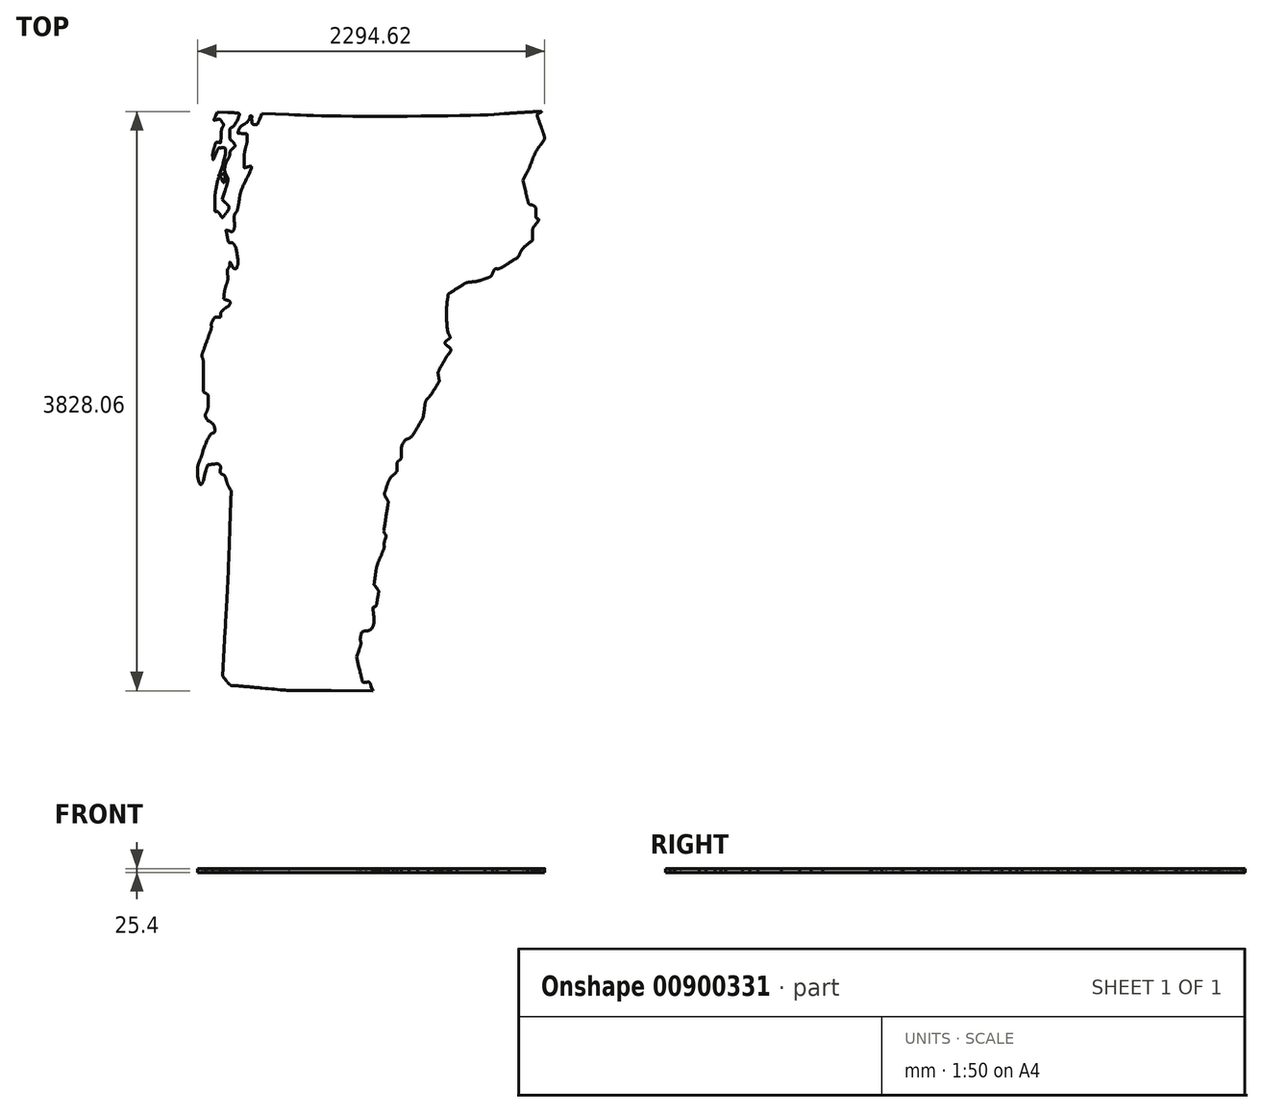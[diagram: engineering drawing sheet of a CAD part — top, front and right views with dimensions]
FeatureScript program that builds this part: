
annotation { "Feature Type Name" : "Feature", "Feature Type Description" : "" }
export const myFeature = defineFeature(function(context is Context, id is Id, definition is map)
    precondition{}
    {
        {
            var Q0;
            Q0=qCreatedBy(makeId("Top.planeOp"),FACE);
            var sketch = newSketch(context, id + "F0", { "sketchPlane" : qUnion([Q0])});
            skLineSegment(sketch, "E0", {"start": v(-2148.42, -1753.94) * mm, "end": v(-2163.83, -1690.8) * mm});
            skLineSegment(sketch, "E1", {"start": v(-2163.83, -1690.8) * mm, "end": v(-2148.01, -1646.42) * mm});
            skLineSegment(sketch, "E2", {"start": v(-1045.74, 1382.66) * mm, "end": v(-1065.36, 1461.75) * mm});
            skLineSegment(sketch, "E3", {"start": v(-1065.36, 1461.75) * mm, "end": v(-1044.06, 1499.75) * mm});
            skLineSegment(sketch, "E4", {"start": v(-2608.76, 1895.1) * mm, "end": v(-2788.04, 1901.18) * mm});
            skLineSegment(sketch, "E5", {"start": v(-2788.04, 1901.18) * mm, "end": v(-2803.72, 1864.08) * mm});
            skLineSegment(sketch, "E6", {"start": v(-3031.83, -1515.3) * mm, "end": v(-3049.52, -1815.66) * mm});
            skLineSegment(sketch, "E7", {"start": v(-3049.52, -1815.66) * mm, "end": v(-3023.97, -1846.84) * mm});
            skLineSegment(sketch, "E8", {"start": v(-2331.5, -1913) * mm, "end": v(-2054.3, -1913.86) * mm});
            skLineSegment(sketch, "E9", {"start": v(-2054.3, -1913.86) * mm, "end": v(-2065.56, -1885.2) * mm});
            skLineSegment(sketch, "E10", {"start": v(-2065.56, -1885.2) * mm, "end": v(-2065.56, -1885.2) * mm});
            skLineSegment(sketch, "E11", {"start": v(-3014.34, 1908.53) * mm, "end": v(-3083.06, 1911.96) * mm});
            skLineSegment(sketch, "E12", {"start": v(-3083.06, 1911.96) * mm, "end": v(-3092.64, 1889.73) * mm});
            skLineSegment(sketch, "E13", {"start": v(-3034.55, 1231.3) * mm, "end": v(-3034.54, 1231.3) * mm});
            skLineSegment(sketch, "E14", {"start": v(-3034.54, 1231.3) * mm, "end": v(-3034.55, 1231.3) * mm});
            skLineSegment(sketch, "E15", {"start": v(-3028.42, 1311.2) * mm, "end": v(-3050.3, 1333.08) * mm});
            skLineSegment(sketch, "E16", {"start": v(-3050.3, 1333.08) * mm, "end": v(-3032, 1390.98) * mm});
            skLineSegment(sketch, "E17", {"start": v(-3014.1, 1468.22) * mm, "end": v(-3030.96, 1512.32) * mm});
            skLineSegment(sketch, "E18", {"start": v(-3030.96, 1512.32) * mm, "end": v(-3014.1, 1468.22) * mm});
            skLineSegment(sketch, "E19", {"start": v(-3017.3, 1591.5) * mm, "end": v(-3017.3, 1591.5) * mm});
            skFitSpline(sketch, "E20", {"points": [v(-2065.56, -1885.2) * mm, v(-2075.06, -1861) * mm, v(-2080.05, -1856.52) * mm, v(-2097.42, -1856.52) * mm]});
            skFitSpline(sketch, "E21", {"points": [v(-2097.42, -1856.52) * mm, v(-2121.49, -1856.52) * mm, v(-2125.24, -1848.98) * mm, v(-2148.42, -1753.94) * mm]});
            skFitSpline(sketch, "E22", {"points": [v(-2148.01, -1646.42) * mm, v(-2139.32, -1622) * mm, v(-2134, -1595.32) * mm, v(-2136.2, -1587.12) * mm]});
            skFitSpline(sketch, "E23", {"points": [v(-2136.2, -1587.12) * mm, v(-2138.4, -1578.92) * mm, v(-2137.39, -1561.34) * mm, v(-2133.95, -1548.06) * mm]});
            skFitSpline(sketch, "E24", {"points": [v(-2133.95, -1548.06) * mm, v(-2129.08, -1529.28) * mm, v(-2122.72, -1522.62) * mm, v(-2105.34, -1518.12) * mm]});
            skFitSpline(sketch, "E25", {"points": [v(-2105.34, -1518.12) * mm, v(-2069.8, -1508.9) * mm, v(-2047.58, -1462.63) * mm, v(-2051.65, -1406.32) * mm]});
            skFitSpline(sketch, "E26", {"points": [v(-2051.65, -1406.32) * mm, v(-2054.2, -1371.05) * mm, v(-2052.62, -1361.24) * mm, v(-2043.8, -1357.86) * mm]});
            skFitSpline(sketch, "E27", {"points": [v(-2043.8, -1357.86) * mm, v(-2036.62, -1355.1) * mm, v(-2029.83, -1336.31) * mm, v(-2024.4, -1304.17) * mm]});
            skFitSpline(sketch, "E28", {"points": [v(-2024.4, -1304.17) * mm, v(-2016.57, -1257.68) * mm, v(-2017, -1253.42) * mm, v(-2031.72, -1232.75) * mm]});
            skFitSpline(sketch, "E29", {"points": [v(-2031.72, -1232.75) * mm, v(-2046.73, -1211.67) * mm, v(-2047.02, -1208.2) * mm, v(-2038.74, -1148.34) * mm]});
            skFitSpline(sketch, "E30", {"points": [v(-2038.74, -1148.34) * mm, v(-2033.05, -1107.24) * mm, v(-2021.43, -1066.31) * mm, v(-2004.72, -1028.56) * mm]});
            skFitSpline(sketch, "E31", {"points": [v(-2004.72, -1028.56) * mm, v(-1990.76, -997.02) * mm, v(-1979.84, -963.26) * mm, v(-1980.45, -953.54) * mm]});
            skFitSpline(sketch, "E32", {"points": [v(-1980.45, -953.54) * mm, v(-1981.06, -943.82) * mm, v(-1978.14, -925.5) * mm, v(-1973.95, -912.84) * mm]});
            skFitSpline(sketch, "E33", {"points": [v(-1973.95, -912.84) * mm, v(-1968.31, -895.74) * mm, v(-1968.62, -886.18) * mm, v(-1975.17, -875.7) * mm]});
            skFitSpline(sketch, "E34", {"points": [v(-1975.17, -875.7) * mm, v(-1982.3, -864.27) * mm, v(-1981.02, -842.87) * mm, v(-1968.46, -763.57) * mm]});
            skFitSpline(sketch, "E35", {"points": [v(-1968.46, -763.57) * mm, v(-1954.46, -675.2) * mm, v(-1953.98, -663.53) * mm, v(-1963.61, -644.9) * mm]});
            skFitSpline(sketch, "E36", {"points": [v(-1963.61, -644.9) * mm, v(-1977.63, -617.8) * mm, v(-1977.12, -606.03) * mm, v(-1959.68, -554.4) * mm]});
            skFitSpline(sketch, "E37", {"points": [v(-1959.68, -554.4) * mm, v(-1950.52, -527.27) * mm, v(-1935.82, -502.16) * mm, v(-1920.26, -487.08) * mm]});
            skFitSpline(sketch, "E38", {"points": [v(-1920.26, -487.08) * mm, v(-1899.8, -467.25) * mm, v(-1895.44, -457.8) * mm, v(-1895.44, -433.29) * mm]});
            skFitSpline(sketch, "E39", {"points": [v(-1895.44, -433.29) * mm, v(-1895.44, -412.65) * mm, v(-1891.05, -399.57) * mm, v(-1881.1, -390.57) * mm]});
            skFitSpline(sketch, "E40", {"points": [v(-1881.1, -390.57) * mm, v(-1870.92, -381.35) * mm, v(-1866.77, -368.5) * mm, v(-1866.77, -346.16) * mm]});
            skFitSpline(sketch, "E41", {"points": [v(-1866.77, -346.16) * mm, v(-1866.77, -307) * mm, v(-1843.82, -260.57) * mm, v(-1816.8, -245.06) * mm]});
            skFitSpline(sketch, "E42", {"points": [v(-1816.8, -245.06) * mm, v(-1804.9, -238.24) * mm, v(-1781.25, -207.78) * mm, v(-1760.1, -172.05) * mm]});
            skFitSpline(sketch, "E43", {"points": [v(-1760.1, -172.05) * mm, v(-1730.1, -121.38) * mm, v(-1722.35, -100.98) * mm, v(-1715.43, -54.43) * mm]});
            skFitSpline(sketch, "E44", {"points": [v(-1715.43, -54.43) * mm, v(-1709.02, -11.34) * mm, v(-1702.54, 7.17) * mm, v(-1687.85, 24.3) * mm]});
            skFitSpline(sketch, "E45", {"points": [v(-1687.85, 24.3) * mm, v(-1677.3, 36.62) * mm, v(-1656.9, 65.75) * mm, v(-1642.55, 89.03) * mm]});
            skFitSpline(sketch, "E46", {"points": [v(-1642.55, 89.03) * mm, v(-1619.85, 125.83) * mm, v(-1617, 135.35) * mm, v(-1620.65, 162) * mm]});
            skFitSpline(sketch, "E47", {"points": [v(-1620.65, 162) * mm, v(-1624.26, 188.36) * mm, v(-1621.07, 199.45) * mm, v(-1597.76, 241.53) * mm]});
            skFitSpline(sketch, "E48", {"points": [v(-1597.76, 241.53) * mm, v(-1582.87, 268.43) * mm, v(-1564.72, 299) * mm, v(-1557.43, 309.46) * mm]});
            skFitSpline(sketch, "E49", {"points": [v(-1557.43, 309.46) * mm, v(-1540.47, 333.83) * mm, v(-1540.72, 346) * mm, v(-1558.52, 362.12) * mm]});
            skFitSpline(sketch, "E50", {"points": [v(-1558.52, 362.12) * mm, v(-1576.84, 378.69) * mm, v(-1576.7, 392.56) * mm, v(-1558.05, 407.65) * mm]});
            skFitSpline(sketch, "E51", {"points": [v(-1558.05, 407.65) * mm, v(-1545, 418.22) * mm, v(-1544.26, 422.18) * mm, v(-1551.79, 441.06) * mm]});
            skFitSpline(sketch, "E52", {"points": [v(-1551.79, 441.06) * mm, v(-1560.89, 463.86) * mm, v(-1567.15, 628.71) * mm, v(-1560.83, 678.8) * mm]});
            skFitSpline(sketch, "E53", {"points": [v(-1560.83, 678.8) * mm, v(-1557.24, 707.23) * mm, v(-1554.07, 710.66) * mm, v(-1498.64, 746) * mm]});
            skFitSpline(sketch, "E54", {"points": [v(-1498.64, 746) * mm, v(-1452.27, 775.56) * mm, v(-1431.38, 784.36) * mm, v(-1397.23, 788.76) * mm]});
            skFitSpline(sketch, "E55", {"points": [v(-1397.23, 788.76) * mm, v(-1373.57, 791.8) * mm, v(-1336.26, 801.1) * mm, v(-1314.32, 809.41) * mm]});
            skFitSpline(sketch, "E56", {"points": [v(-1314.32, 809.41) * mm, v(-1282.53, 821.45) * mm, v(-1271.99, 829.62) * mm, v(-1262.46, 849.6) * mm]});
            skFitSpline(sketch, "E57", {"points": [v(-1262.46, 849.6) * mm, v(-1254.04, 867.25) * mm, v(-1245.7, 874.7) * mm, v(-1234.26, 874.78) * mm]});
            skFitSpline(sketch, "E58", {"points": [v(-1234.26, 874.78) * mm, v(-1225.33, 874.85) * mm, v(-1190.6, 892.04) * mm, v(-1157.09, 913) * mm]});
            skFitSpline(sketch, "E59", {"points": [v(-1157.09, 913) * mm, v(-1109.24, 942.9) * mm, v(-1093.08, 957.4) * mm, v(-1081.82, 980.47) * mm]});
            skFitSpline(sketch, "E60", {"points": [v(-1081.82, 980.47) * mm, v(-1073.93, 996.64) * mm, v(-1052.17, 1022.18) * mm, v(-1033.46, 1037.24) * mm]});
            skFitSpline(sketch, "E61", {"points": [v(-1033.46, 1037.24) * mm, v(-1000.4, 1063.85) * mm, v(-999.43, 1065.74) * mm, v(-999.2, 1104.05) * mm]});
            skFitSpline(sketch, "E62", {"points": [v(-999.2, 1104.05) * mm, v(-999.02, 1136.53) * mm, v(-995.2, 1148.47) * mm, v(-977.56, 1171.8) * mm]});
            skFitSpline(sketch, "E63", {"points": [v(-977.56, 1171.8) * mm, v(-959.49, 1195.68) * mm, v(-957.83, 1201.07) * mm, v(-967, 1206.2) * mm]});
            skFitSpline(sketch, "E64", {"points": [v(-967, 1206.2) * mm, v(-974.09, 1210.17) * mm, v(-977.88, 1223.01) * mm, v(-977.88, 1243.08) * mm]});
            skFitSpline(sketch, "E65", {"points": [v(-977.88, 1243.08) * mm, v(-977.88, 1273.86) * mm, v(-988.6, 1290.36) * mm, v(-1014.54, 1299.5) * mm]});
            skFitSpline(sketch, "E66", {"points": [v(-1014.54, 1299.5) * mm, v(-1022.4, 1302.27) * mm, v(-1032.41, 1328.94) * mm, v(-1045.74, 1382.66) * mm]});
            skFitSpline(sketch, "E67", {"points": [v(-1044.06, 1499.75) * mm, v(-1032.34, 1520.64) * mm, v(-1013.81, 1561.94) * mm, v(-1002.88, 1591.5) * mm]});
            skFitSpline(sketch, "E68", {"points": [v(-1002.88, 1591.5) * mm, v(-991.95, 1621.07) * mm, v(-968.95, 1664.42) * mm, v(-951.77, 1687.83) * mm]});
            skFitSpline(sketch, "E69", {"points": [v(-951.77, 1687.83) * mm, v(-934.58, 1711.24) * mm, v(-920.53, 1734.37) * mm, v(-920.53, 1739.23) * mm]});
            skFitSpline(sketch, "E70", {"points": [v(-920.53, 1739.23) * mm, v(-920.53, 1744.1) * mm, v(-930.2, 1775.49) * mm, v(-942.03, 1809) * mm]});
            skFitSpline(sketch, "E71", {"points": [v(-942.03, 1809) * mm, v(-966.83, 1879.25) * mm, v(-968.4, 1896.2) * mm, v(-951, 1906.34) * mm]});
            skFitSpline(sketch, "E72", {"points": [v(-951, 1906.34) * mm, v(-940.05, 1912.71) * mm, v(-940.74, 1913.68) * mm, v(-956.37, 1913.86) * mm]});
            skFitSpline(sketch, "E73", {"points": [v(-956.37, 1913.86) * mm, v(-966.23, 1913.99) * mm, v(-1056.4, 1909.13) * mm, v(-1156.75, 1903.07) * mm]});
            skFitSpline(sketch, "E74", {"points": [v(-1156.75, 1903.07) * mm, v(-1368.69, 1890.3) * mm, v(-2314.58, 1885.09) * mm, v(-2608.76, 1895.1) * mm]});
            skFitSpline(sketch, "E75", {"points": [v(-2803.72, 1864.08) * mm, v(-2816.9, 1832.88) * mm, v(-2822.03, 1827.34) * mm, v(-2835.91, 1829.3) * mm]});
            skFitSpline(sketch, "E76", {"points": [v(-2835.91, 1829.3) * mm, v(-2849.08, 1831.17) * mm, v(-2853.15, 1837.2) * mm, v(-2856, 1859.1) * mm]});
            skFitSpline(sketch, "E77", {"points": [v(-2872.23, 1865) * mm, v(-2879.18, 1853.15) * mm, v(-2895.83, 1836.68) * mm, v(-2909.23, 1828.4) * mm]});
            skFitSpline(sketch, "E78", {"points": [v(-2909.23, 1828.4) * mm, v(-2922.63, 1820.12) * mm, v(-2936.88, 1803.92) * mm, v(-2940.89, 1792.42) * mm]});
            skFitSpline(sketch, "E79", {"points": [v(-2940.89, 1792.42) * mm, v(-2948.13, 1771.64) * mm, v(-2947.97, 1771.48) * mm, v(-2918.22, 1769.31) * mm]});
            skFitSpline(sketch, "E80", {"points": [v(-2918.22, 1769.31) * mm, v(-2890.43, 1767.29) * mm, v(-2888.1, 1765.5) * mm, v(-2886.08, 1744.6) * mm]});
            skFitSpline(sketch, "E81", {"points": [v(-2886.08, 1744.6) * mm, v(-2884.87, 1732.22) * mm, v(-2888.9, 1702.72) * mm, v(-2895.04, 1679.06) * mm]});
            skFitSpline(sketch, "E82", {"points": [v(-2895.04, 1679.06) * mm, v(-2901.17, 1655.4) * mm, v(-2906.19, 1615.17) * mm, v(-2906.19, 1589.67) * mm]});
            skFitSpline(sketch, "E83", {"points": [v(-2906.19, 1589.67) * mm, v(-2906.19, 1544.15) * mm, v(-2905.86, 1543.38) * mm, v(-2888.36, 1546.72) * mm]});
            skFitSpline(sketch, "E84", {"points": [v(-2888.36, 1546.72) * mm, v(-2858.93, 1552.35) * mm, v(-2860.45, 1533.85) * mm, v(-2895.66, 1458.28) * mm]});
            skFitSpline(sketch, "E85", {"points": [v(-2895.66, 1458.28) * mm, v(-2919.3, 1407.5) * mm, v(-2931.76, 1368.85) * mm, v(-2939.26, 1322.95) * mm]});
            skFitSpline(sketch, "E86", {"points": [v(-2939.26, 1322.95) * mm, v(-2945.03, 1287.6) * mm, v(-2954.47, 1253.48) * mm, v(-2960.23, 1247.11) * mm]});
            skFitSpline(sketch, "E87", {"points": [v(-2960.23, 1247.11) * mm, v(-2966.86, 1239.78) * mm, v(-2970.79, 1219.98) * mm, v(-2970.93, 1193.1) * mm]});
            skFitSpline(sketch, "E88", {"points": [v(-2970.93, 1193.1) * mm, v(-2971.2, 1143.34) * mm, v(-2983.25, 1122.17) * mm, v(-3008.54, 1127) * mm]});
            skFitSpline(sketch, "E89", {"points": [v(-3008.54, 1127) * mm, v(-3025.55, 1130.26) * mm, v(-3025.56, 1130.23) * mm, v(-3017.58, 1090.27) * mm]});
            skFitSpline(sketch, "E90", {"points": [v(-3017.58, 1090.27) * mm, v(-3011.03, 1057.45) * mm, v(-3006.75, 1049.88) * mm, v(-2993.72, 1048) * mm]});
            skFitSpline(sketch, "E91", {"points": [v(-2993.72, 1048) * mm, v(-2984.99, 1046.73) * mm, v(-2974.9, 1040.2) * mm, v(-2971.3, 1033.5) * mm]});
            skFitSpline(sketch, "E92", {"points": [v(-2971.3, 1033.5) * mm, v(-2961.65, 1015.46) * mm, v(-2946.27, 906.96) * mm, v(-2951.45, 893.46) * mm]});
            skFitSpline(sketch, "E93", {"points": [v(-2951.45, 893.46) * mm, v(-2958.29, 875.65) * mm, v(-2976.2, 879.6) * mm, v(-2988.1, 901.54) * mm]});
            skFitSpline(sketch, "E94", {"points": [v(-2988.1, 901.54) * mm, v(-2997.18, 918.27) * mm, v(-2998.88, 919.08) * mm, v(-2999.32, 906.92) * mm]});
            skFitSpline(sketch, "E95", {"points": [v(-2999.32, 906.92) * mm, v(-2999.6, 899.03) * mm, v(-3004.17, 886.87) * mm, v(-3009.46, 879.9) * mm]});
            skFitSpline(sketch, "E96", {"points": [v(-3009.46, 879.9) * mm, v(-3015.64, 871.75) * mm, v(-3017.83, 856) * mm, v(-3015.56, 835.9) * mm]});
            skFitSpline(sketch, "E97", {"points": [v(-3015.56, 835.9) * mm, v(-3013.43, 817.02) * mm, v(-3016.63, 790.73) * mm, v(-3023.6, 769.73) * mm]});
            skFitSpline(sketch, "E98", {"points": [v(-3023.6, 769.73) * mm, v(-3029.96, 750.56) * mm, v(-3036.43, 721.77) * mm, v(-3037.97, 705.76) * mm]});
            skFitSpline(sketch, "E99", {"points": [v(-3037.97, 705.76) * mm, v(-3040.3, 681.44) * mm, v(-3038.25, 675.54) * mm, v(-3025.49, 669.92) * mm]});
            skFitSpline(sketch, "E100", {"points": [v(-3025.49, 669.92) * mm, v(-2999.78, 658.6) * mm, v(-3002.3, 638.08) * mm, v(-3032.5, 612.72) * mm]});
            skFitSpline(sketch, "E101", {"points": [v(-3032.5, 612.72) * mm, v(-3049.94, 598.09) * mm, v(-3060.03, 583.45) * mm, v(-3060.14, 572.66) * mm]});
            skFitSpline(sketch, "E102", {"points": [v(-3060.14, 572.66) * mm, v(-3060.28, 558.85) * mm, v(-3064.15, 555.61) * mm, v(-3080.83, 555.37) * mm]});
            skFitSpline(sketch, "E103", {"points": [v(-3080.83, 555.37) * mm, v(-3096.07, 555.16) * mm, v(-3104.27, 549.62) * mm, v(-3112.7, 533.87) * mm]});
            skFitSpline(sketch, "E104", {"points": [v(-3112.7, 533.87) * mm, v(-3118.95, 522.2) * mm, v(-3123.31, 506.2) * mm, v(-3122.4, 498.32) * mm]});
            skFitSpline(sketch, "E105", {"points": [v(-3122.4, 498.32) * mm, v(-3121.5, 490.43) * mm, v(-3135.56, 443.78) * mm, v(-3153.65, 394.64) * mm]});
            skFitSpline(sketch, "E106", {"points": [v(-3153.65, 394.64) * mm, v(-3178.45, 327.3) * mm, v(-3185.13, 300.82) * mm, v(-3180.8, 287.11) * mm]});
            skFitSpline(sketch, "E107", {"points": [v(-3180.8, 287.11) * mm, v(-3177.65, 277.11) * mm, v(-3175.06, 222.57) * mm, v(-3175.04, 165.91) * mm]});
            skFitSpline(sketch, "E108", {"points": [v(-3175.04, 165.91) * mm, v(-3174.97, 67.07) * mm, v(-3174.35, 62.46) * mm, v(-3158.88, 52.13) * mm]});
            skFitSpline(sketch, "E109", {"points": [v(-3158.88, 52.13) * mm, v(-3145.18, 43) * mm, v(-3142.75, 34.97) * mm, v(-3142.75, -1) * mm]});
            skFitSpline(sketch, "E110", {"points": [v(-3142.75, -1) * mm, v(-3142.75, -24.3) * mm, v(-3147.47, -54.66) * mm, v(-3153.23, -68.46) * mm]});
            skFitSpline(sketch, "E111", {"points": [v(-3153.23, -68.46) * mm, v(-3161.37, -87.94) * mm, v(-3161.92, -97.53) * mm, v(-3155.67, -111.24) * mm]});
            skFitSpline(sketch, "E112", {"points": [v(-3155.67, -111.24) * mm, v(-3151.24, -120.97) * mm, v(-3144.9, -128.92) * mm, v(-3141.6, -128.92) * mm]});
            skFitSpline(sketch, "E113", {"points": [v(-3141.6, -128.92) * mm, v(-3138.29, -128.92) * mm, v(-3129.13, -135.37) * mm, v(-3121.24, -143.26) * mm]});
            skFitSpline(sketch, "E114", {"points": [v(-3121.24, -143.26) * mm, v(-3106.41, -158.09) * mm, v(-3101.18, -203.4) * mm, v(-3113.43, -210.96) * mm]});
            skFitSpline(sketch, "E115", {"points": [v(-3113.43, -210.96) * mm, v(-3128.05, -220) * mm, v(-3172.72, -312.7) * mm, v(-3186.3, -362.22) * mm]});
            skFitSpline(sketch, "E116", {"points": [v(-3186.3, -362.22) * mm, v(-3214.8, -466.07) * mm, v(-3192.38, -550.53) * mm, v(-3160.18, -460.64) * mm]});
            skFitSpline(sketch, "E117", {"points": [v(-3160.18, -460.64) * mm, v(-3145.43, -419.46) * mm, v(-3145.19, -419.23) * mm, v(-3113.84, -416.96) * mm]});
            skFitSpline(sketch, "E118", {"points": [v(-3113.84, -416.96) * mm, v(-3078.46, -414.4) * mm, v(-3063.9, -426.47) * mm, v(-3063.9, -458.34) * mm]});
            skFitSpline(sketch, "E119", {"points": [v(-3063.9, -458.34) * mm, v(-3063.9, -470.28) * mm, v(-3058.43, -479.27) * mm, v(-3048.4, -483.85) * mm]});
            skFitSpline(sketch, "E120", {"points": [v(-3048.4, -483.85) * mm, v(-3039.2, -488.05) * mm, v(-3029.49, -502.6) * mm, v(-3024.51, -519.6) * mm]});
            skFitSpline(sketch, "E121", {"points": [v(-3024.51, -519.6) * mm, v(-3019.9, -535.37) * mm, v(-3010.46, -559.15) * mm, v(-3003.54, -572.43) * mm]});
            skFitSpline(sketch, "E122", {"points": [v(-3003.54, -572.43) * mm, v(-2991.58, -595.39) * mm, v(-2991.53, -611.96) * mm, v(-3002.54, -905.76) * mm]});
            skFitSpline(sketch, "E123", {"points": [v(-3002.54, -905.76) * mm, v(-3008.92, -1075.81) * mm, v(-3022.1, -1350.1) * mm, v(-3031.83, -1515.3) * mm]});
            skFitSpline(sketch, "E124", {"points": [v(-2856, 1859.1) * mm, v(-2857.2, 1868.26) * mm, v(-2853.05, 1883.64) * mm, v(-2859.6, 1886.56) * mm]});
            skFitSpline(sketch, "E125", {"points": [v(-2859.6, 1886.56) * mm, v(-2865.02, 1886.68) * mm, v(-2868.03, 1872.28) * mm, v(-2872.23, 1865) * mm]});
            skFitSpline(sketch, "E126", {"points": [v(-3023.97, -1846.84) * mm, v(-3008.68, -1865.5) * mm, v(-2992.13, -1878.24) * mm, v(-2982.77, -1878.57) * mm]});
            skFitSpline(sketch, "E127", {"points": [v(-2982.77, -1878.57) * mm, v(-2974.16, -1878.87) * mm, v(-2886.47, -1886.54) * mm, v(-2787.9, -1895.63) * mm]});
            skFitSpline(sketch, "E128", {"points": [v(-2787.9, -1895.63) * mm, v(-2640.68, -1909.2) * mm, v(-2559.23, -1912.3) * mm, v(-2331.5, -1913) * mm]});
            skFitSpline(sketch, "E129", {"points": [v(-3017.3, 1591.5) * mm, v(-3007.44, 1610.96) * mm, v(-2999.38, 1632.87) * mm, v(-2999.38, 1640.2) * mm]});
            skFitSpline(sketch, "E130", {"points": [v(-2999.38, 1640.2) * mm, v(-2999.38, 1647.53) * mm, v(-2991.44, 1660.98) * mm, v(-2981.74, 1670.1) * mm]});
            skFitSpline(sketch, "E131", {"points": [v(-2981.74, 1670.1) * mm, v(-2966.97, 1683.97) * mm, v(-2965.39, 1689.14) * mm, v(-2972.03, 1701.81) * mm]});
            skFitSpline(sketch, "E132", {"points": [v(-2972.03, 1701.81) * mm, v(-2976.4, 1710.14) * mm, v(-2984.34, 1719.53) * mm, v(-2989.67, 1722.69) * mm]});
            skFitSpline(sketch, "E133", {"points": [v(-2989.67, 1722.69) * mm, v(-2995.86, 1726.34) * mm, v(-2999.38, 1741.96) * mm, v(-2999.38, 1765.76) * mm]});
            skFitSpline(sketch, "E134", {"points": [v(-2999.38, 1765.76) * mm, v(-2999.38, 1794.76) * mm, v(-2996.32, 1805.02) * mm, v(-2985.69, 1811.66) * mm]});
            skFitSpline(sketch, "E135", {"points": [v(-2985.69, 1811.66) * mm, v(-2974.04, 1818.94) * mm, v(-2937.59, 1898.3) * mm, v(-2943.57, 1903.36) * mm]});
            skFitSpline(sketch, "E136", {"points": [v(-2943.57, 1903.36) * mm, v(-2944.7, 1904.31) * mm, v(-2976.54, 1906.64) * mm, v(-3014.34, 1908.53) * mm]});
            skFitSpline(sketch, "E137", {"points": [v(-3092.64, 1889.73) * mm, v(-3097.9, 1877.5) * mm, v(-3103.53, 1865.1) * mm, v(-3105.14, 1862.18) * mm]});
            skFitSpline(sketch, "E138", {"points": [v(-3105.14, 1862.18) * mm, v(-3106.74, 1859.26) * mm, v(-3098.42, 1858.8) * mm, v(-3086.64, 1861.15) * mm]});
            skFitSpline(sketch, "E139", {"points": [v(-3086.64, 1861.15) * mm, v(-3068.89, 1864.7) * mm, v(-3063.1, 1862.18) * mm, v(-3052.77, 1846.42) * mm]});
            skFitSpline(sketch, "E140", {"points": [v(-3052.77, 1846.42) * mm, v(-3042.82, 1831.23) * mm, v(-3041.94, 1824.24) * mm, v(-3048.4, 1811.6) * mm]});
            skFitSpline(sketch, "E141", {"points": [v(-3048.4, 1811.6) * mm, v(-3052.85, 1802.92) * mm, v(-3057.35, 1776.45) * mm, v(-3058.4, 1752.8) * mm]});
            skFitSpline(sketch, "E142", {"points": [v(-3058.4, 1752.8) * mm, v(-3060.16, 1713.21) * mm, v(-3061.6, 1709.83) * mm, v(-3076.6, 1710.37) * mm]});
            skFitSpline(sketch, "E143", {"points": [v(-3076.6, 1710.37) * mm, v(-3090.25, 1710.86) * mm, v(-3094.66, 1704.8) * mm, v(-3103.96, 1672.82) * mm]});
            skFitSpline(sketch, "E144", {"points": [v(-3103.96, 1672.82) * mm, v(-3110.06, 1651.84) * mm, v(-3113.91, 1625.78) * mm, v(-3112.53, 1614.89) * mm]});
            skFitSpline(sketch, "E145", {"points": [v(-3112.53, 1614.89) * mm, v(-3110.07, 1595.6) * mm, v(-3109.7, 1595.83) * mm, v(-3097.78, 1623.76) * mm]});
            skFitSpline(sketch, "E146", {"points": [v(-3097.78, 1623.76) * mm, v(-3079.17, 1667.4) * mm, v(-3074.21, 1673.94) * mm, v(-3059.73, 1673.94) * mm]});
            skFitSpline(sketch, "E147", {"points": [v(-3059.73, 1673.94) * mm, v(-3032.69, 1673.94) * mm, v(-3040.57, 1586.5) * mm, v(-3067.82, 1503.6) * mm]});
            skFitSpline(sketch, "E148", {"points": [v(-3067.82, 1503.6) * mm, v(-3072.77, 1488.72) * mm, v(-3053.63, 1496.76) * mm, v(-3043.6, 1504) * mm]});
            skFitSpline(sketch, "E149", {"points": [v(-3043.6, 1504) * mm, v(-3037.26, 1502.4) * mm, v(-3035.97, 1498.87) * mm, v(-3035.68, 1494.97) * mm]});
            skFitSpline(sketch, "E150", {"points": [v(-3035.68, 1494.97) * mm, v(-3031.48, 1480.16) * mm, v(-3039.94, 1445.2) * mm, v(-3047.15, 1455.3) * mm]});
            skFitSpline(sketch, "E151", {"points": [v(-3047.15, 1455.3) * mm, v(-3068.01, 1484.52) * mm, v(-3087.08, 1427.97) * mm, v(-3093.14, 1396.6) * mm]});
            skFitSpline(sketch, "E152", {"points": [v(-3093.14, 1396.6) * mm, v(-3096.43, 1379.6) * mm, v(-3099.26, 1340.7) * mm, v(-3099.43, 1310.15) * mm]});
            skFitSpline(sketch, "E153", {"points": [v(-3099.43, 1310.15) * mm, v(-3099.68, 1265.79) * mm, v(-3097.6, 1254.6) * mm, v(-3089.15, 1254.6) * mm]});
            skFitSpline(sketch, "E154", {"points": [v(-3089.15, 1254.6) * mm, v(-3083.33, 1254.6) * mm, v(-3073.28, 1246.53) * mm, v(-3066.82, 1236.67) * mm]});
            skFitSpline(sketch, "E155", {"points": [v(-3066.82, 1236.67) * mm, v(-3052.9, 1215.42) * mm, v(-3047.95, 1214.6) * mm, v(-3034.55, 1231.3) * mm]});
            skFitSpline(sketch, "E156", {"points": [v(-3034.54, 1231.3) * mm, v(-3020.73, 1248.49) * mm, v(-3006.55, 1274.5) * mm, v(-3006.55, 1282.62) * mm]});
            skFitSpline(sketch, "E157", {"points": [v(-3006.55, 1282.62) * mm, v(-3006.55, 1286.3) * mm, v(-3016.4, 1299.17) * mm, v(-3028.42, 1311.2) * mm]});
            skFitSpline(sketch, "E158", {"points": [v(-3032, 1390.98) * mm, v(-3021.95, 1422.82) * mm, v(-3013.89, 1457.58) * mm, v(-3014.1, 1468.22) * mm]});
            skFitSpline(sketch, "E159", {"points": [v(-3030.96, 1512.32) * mm, v(-3034.77, 1529.73) * mm, v(-3027.16, 1572.06) * mm, v(-3017.3, 1591.5) * mm]});
            skLineSegment(sketch, "E160", {"start": v(611.4, -2208.99) * mm, "end": v(647.03, -2208.99) * mm});
            skLineSegment(sketch, "E161", {"start": v(647.03, -2208.99) * mm, "end": v(647.03, -2171.07) * mm});
            skLineSegment(sketch, "E162", {"start": v(1319.35, -1727.03) * mm, "end": v(1337.41, -1705.52) * mm});
            skLineSegment(sketch, "E163", {"start": v(1337.41, -1705.52) * mm, "end": v(1309.43, -1701.94) * mm});
            skLineSegment(sketch, "E164", {"start": v(-594.37, 211.36) * mm, "end": v(-609.97, 203.01) * mm});
            skLineSegment(sketch, "E165", {"start": v(-609.97, 203.01) * mm, "end": v(-591.64, 193.4) * mm});
            skLineSegment(sketch, "E166", {"start": v(-1257.97, -1843.47) * mm, "end": v(-1299.2, -1857.18) * mm});
            skLineSegment(sketch, "E167", {"start": v(-1299.2, -1857.18) * mm, "end": v(-1302.78, -1904.43) * mm});
            skFitSpline(sketch, "E168", {"points": [v(514.3, -2264.34) * mm, v(551, -2219.55) * mm, v(569.53, -2208.99) * mm, v(611.4, -2208.99) * mm]});
            skFitSpline(sketch, "E169", {"points": [v(647.03, -2171.07) * mm, v(647.03, -2090.85) * mm, v(705.3, -2063.24) * mm, v(813.22, -2092.33) * mm]});
            skFitSpline(sketch, "E170", {"points": [v(813.22, -2092.33) * mm, v(831.1, -2097.15) * mm, v(833.56, -2094.93) * mm, v(848.3, -2060.67) * mm]});
            skFitSpline(sketch, "E171", {"points": [v(848.3, -2060.67) * mm, v(865.81, -2019.96) * mm, v(884.85, -2006.3) * mm, v(934.81, -1998.62) * mm]});
            skFitSpline(sketch, "E172", {"points": [v(934.81, -1998.62) * mm, v(951.98, -1995.97) * mm, v(981.93, -1985.86) * mm, v(1001.36, -1976.14) * mm]});
            skFitSpline(sketch, "E173", {"points": [v(1001.36, -1976.14) * mm, v(1046, -1953.8) * mm, v(1108.15, -1955.6) * mm, v(1141.39, -1980.17) * mm]});
            skFitSpline(sketch, "E174", {"points": [v(1141.39, -1980.17) * mm, v(1153.04, -1988.8) * mm, v(1168.05, -1995.84) * mm, v(1174.74, -1995.84) * mm]});
            skFitSpline(sketch, "E175", {"points": [v(1174.74, -1995.84) * mm, v(1186.1, -1995.84) * mm, v(1186.09, -1994.96) * mm, v(1174.55, -1982.21) * mm]});
            skFitSpline(sketch, "E176", {"points": [v(1174.55, -1982.21) * mm, v(1166.25, -1973.03) * mm, v(1162.95, -1959.56) * mm, v(1164.48, -1941) * mm]});
            skFitSpline(sketch, "E177", {"points": [v(1164.48, -1941) * mm, v(1166.7, -1914.02) * mm, v(1167.38, -1913.4) * mm, v(1195.11, -1913.4) * mm]});
            skFitSpline(sketch, "E178", {"points": [v(1195.11, -1913.4) * mm, v(1221.15, -1913.4) * mm, v(1223.86, -1911.56) * mm, v(1228.1, -1890.93) * mm]});
            skFitSpline(sketch, "E179", {"points": [v(1228.1, -1890.93) * mm, v(1230.63, -1878.57) * mm, v(1239.22, -1859.22) * mm, v(1247.2, -1847.92) * mm]});
            skFitSpline(sketch, "E180", {"points": [v(1247.2, -1847.92) * mm, v(1255.16, -1836.63) * mm, v(1270.6, -1809.64) * mm, v(1281.48, -1787.96) * mm]});
            skFitSpline(sketch, "E181", {"points": [v(1281.48, -1787.96) * mm, v(1292.38, -1766.27) * mm, v(1309.42, -1738.86) * mm, v(1319.35, -1727.03) * mm]});
            skFitSpline(sketch, "E182", {"points": [v(1309.43, -1701.94) * mm, v(1286.97, -1699.06) * mm, v(1280.98, -1695.09) * mm, v(1279.1, -1681.83) * mm]});
            skFitSpline(sketch, "E183", {"points": [v(1279.1, -1681.83) * mm, v(1277.81, -1672.74) * mm, v(1280.35, -1660.97) * mm, v(1284.75, -1655.67) * mm]});
            skFitSpline(sketch, "E184", {"points": [v(1284.75, -1655.67) * mm, v(1291.06, -1648.07) * mm, v(1284.06, -1640.6) * mm, v(1251.48, -1620.23) * mm]});
            skFitSpline(sketch, "E185", {"points": [v(1251.48, -1620.23) * mm, v(1205.64, -1591.56) * mm, v(1188.73, -1588.43) * mm, v(1178.5, -1606.72) * mm]});
            skFitSpline(sketch, "E186", {"points": [v(1178.5, -1606.72) * mm, v(1173.23, -1616.11) * mm, v(1175.81, -1622.94) * mm, v(1189.37, -1635.5) * mm]});
            skFitSpline(sketch, "E187", {"points": [v(1189.37, -1635.5) * mm, v(1226.12, -1669.56) * mm, v(1194.8, -1706.62) * mm, v(1140.84, -1692.93) * mm]});
            skFitSpline(sketch, "E188", {"points": [v(1140.84, -1692.93) * mm, v(1117.4, -1686.98) * mm, v(1108.02, -1688.01) * mm, v(1088.12, -1698.73) * mm]});
            skFitSpline(sketch, "E189", {"points": [v(1088.12, -1698.73) * mm, v(1067.94, -1709.6) * mm, v(1062.02, -1710.21) * mm, v(1052.6, -1702.4) * mm]});
            skFitSpline(sketch, "E190", {"points": [v(1052.6, -1702.4) * mm, v(1032.92, -1686.06) * mm, v(1038.66, -1652.57) * mm, v(1065.42, -1627.64) * mm]});
            skFitSpline(sketch, "E191", {"points": [v(1065.42, -1627.64) * mm, v(1094.7, -1600.35) * mm, v(1108.82, -1575.6) * mm, v(1098.67, -1569.33) * mm]});
            skFitSpline(sketch, "E192", {"points": [v(1098.67, -1569.33) * mm, v(1094.71, -1566.9) * mm, v(1091.48, -1556.94) * mm, v(1091.48, -1547.22) * mm]});
            skFitSpline(sketch, "E193", {"points": [v(1091.48, -1547.22) * mm, v(1091.48, -1527.66) * mm, v(1113.33, -1515.56) * mm, v(1148.62, -1515.56) * mm]});
            skFitSpline(sketch, "E194", {"points": [v(1148.62, -1515.56) * mm, v(1167.77, -1515.56) * mm, v(1169.29, -1513.31) * mm, v(1174.01, -1477.92) * mm]});
            skFitSpline(sketch, "E195", {"points": [v(1174.01, -1477.92) * mm, v(1176.78, -1457.22) * mm, v(1183.14, -1435.45) * mm, v(1188.15, -1429.54) * mm]});
            skFitSpline(sketch, "E196", {"points": [v(1188.15, -1429.54) * mm, v(1193.16, -1423.62) * mm, v(1198.62, -1408.87) * mm, v(1200.29, -1396.75) * mm]});
            skFitSpline(sketch, "E197", {"points": [v(1200.29, -1396.75) * mm, v(1202.84, -1378.16) * mm, v(1199.47, -1372.01) * mm, v(1178.63, -1357.33) * mm]});
            skFitSpline(sketch, "E198", {"points": [v(1178.63, -1357.33) * mm, v(1157.83, -1342.68) * mm, v(1122.4, -1312.03) * mm, v(1072.96, -1265.94) * mm]});
            skFitSpline(sketch, "E199", {"points": [v(1072.96, -1265.94) * mm, v(1067.38, -1260.73) * mm, v(1062.8, -1249.25) * mm, v(1062.8, -1240.43) * mm]});
            skFitSpline(sketch, "E200", {"points": [v(1062.8, -1240.43) * mm, v(1062.8, -1215.34) * mm, v(1046.84, -1199.49) * mm, v(1008.77, -1186.78) * mm]});
            skFitSpline(sketch, "E201", {"points": [v(1008.77, -1186.78) * mm, v(976.85, -1176.12) * mm, v(972.4, -1171.82) * mm, v(959.51, -1139.21) * mm]});
            skFitSpline(sketch, "E202", {"points": [v(959.51, -1139.21) * mm, v(940.89, -1092.08) * mm, v(941.82, -1045.62) * mm, v(962.23, -1003.46) * mm]});
            skFitSpline(sketch, "E203", {"points": [v(962.23, -1003.46) * mm, v(971.22, -984.9) * mm, v(977.97, -961.87) * mm, v(977.23, -952.3) * mm]});
            skFitSpline(sketch, "E204", {"points": [v(977.23, -952.3) * mm, v(974.71, -919.75) * mm, v(975.6, -902.7) * mm, v(982.52, -850.8) * mm]});
            skFitSpline(sketch, "E205", {"points": [v(982.52, -850.8) * mm, v(988.46, -806.25) * mm, v(987.62, -795.14) * mm, v(976.55, -771.95) * mm]});
            skFitSpline(sketch, "E206", {"points": [v(976.55, -771.95) * mm, v(958.8, -734.73) * mm, v(949.56, -600.06) * mm, v(923.09, 7.74) * mm]});
            skFitSpline(sketch, "E207", {"points": [v(923.09, 7.74) * mm, v(921.03, 55.05) * mm, v(917.73, 127.63) * mm, v(915.75, 169.03) * mm]});
            skFitSpline(sketch, "E208", {"points": [v(915.75, 169.03) * mm, v(913.78, 210.42) * mm, v(908.98, 323.33) * mm, v(905.09, 419.92) * mm]});
            skFitSpline(sketch, "E209", {"points": [v(905.09, 419.92) * mm, v(901.2, 516.52) * mm, v(896.36, 631.03) * mm, v(894.35, 674.4) * mm]});
            skFitSpline(sketch, "E210", {"points": [v(894.35, 674.4) * mm, v(892.34, 717.77) * mm, v(885.92, 856.48) * mm, v(880.09, 982.64) * mm]});
            skFitSpline(sketch, "E211", {"points": [v(880.09, 982.64) * mm, v(874.26, 1108.8) * mm, v(867.72, 1244.3) * mm, v(865.57, 1283.72) * mm]});
            skFitSpline(sketch, "E212", {"points": [v(865.57, 1283.72) * mm, v(853.87, 1498.13) * mm, v(811.8, 2221.17) * mm, v(809.14, 2253.81) * mm]});
            skFitSpline(sketch, "E213", {"points": [v(809.14, 2253.81) * mm, v(805.72, 2295.55) * mm, v(797.71, 2313) * mm, v(797.33, 2279.54) * mm]});
            skFitSpline(sketch, "E214", {"points": [v(797.33, 2279.54) * mm, v(797.2, 2268.04) * mm, v(788.16, 2245.72) * mm, v(777.23, 2229.95) * mm]});
            skFitSpline(sketch, "E215", {"points": [v(777.23, 2229.95) * mm, v(758.87, 2203.44) * mm, v(754.7, 2201.2) * mm, v(721.92, 2200.19) * mm]});
            skFitSpline(sketch, "E216", {"points": [v(721.92, 2200.19) * mm, v(645, 2197.82) * mm, v(604, 2205.69) * mm, v(580.27, 2227.37) * mm]});
            skFitSpline(sketch, "E217", {"points": [v(580.27, 2227.37) * mm, v(567.92, 2238.65) * mm, v(555.7, 2247.88) * mm, v(553.12, 2247.88) * mm]});
            skFitSpline(sketch, "E218", {"points": [v(553.12, 2247.88) * mm, v(550.53, 2247.88) * mm, v(544.4, 2257.55) * mm, v(539.5, 2269.38) * mm]});
            skFitSpline(sketch, "E219", {"points": [v(539.5, 2269.38) * mm, v(528.37, 2296.26) * mm, v(519.8, 2296.26) * mm, v(477.42, 2269.38) * mm]});
            skFitSpline(sketch, "E220", {"points": [v(477.42, 2269.38) * mm, v(458.77, 2257.55) * mm, v(439.3, 2247.88) * mm, v(434.16, 2247.88) * mm]});
            skFitSpline(sketch, "E221", {"points": [v(434.16, 2247.88) * mm, v(429.02, 2247.88) * mm, v(424.81, 2240.99) * mm, v(424.81, 2232.57) * mm]});
            skFitSpline(sketch, "E222", {"points": [v(424.81, 2232.57) * mm, v(424.81, 2224.15) * mm, v(416.17, 2209.25) * mm, v(405.6, 2199.46) * mm]});
            skFitSpline(sketch, "E223", {"points": [v(405.6, 2199.46) * mm, v(388.77, 2183.86) * mm, v(381.92, 2182.17) * mm, v(350.05, 2185.74) * mm]});
            skFitSpline(sketch, "E224", {"points": [v(350.05, 2185.74) * mm, v(314.84, 2189.68) * mm, v(314.32, 2189.48) * mm, v(333.32, 2179.23) * mm]});
            skFitSpline(sketch, "E225", {"points": [v(333.32, 2179.23) * mm, v(363.31, 2163.07) * mm, v(364.79, 2141.06) * mm, v(339.44, 2087.95) * mm]});
            skFitSpline(sketch, "E226", {"points": [v(339.44, 2087.95) * mm, v(322.8, 2053.09) * mm, v(318.45, 2035.98) * mm, v(321.86, 2018.9) * mm]});
            skFitSpline(sketch, "E227", {"points": [v(321.86, 2018.9) * mm, v(325.46, 2000.91) * mm, v(322.76, 1992.2) * mm, v(308.81, 1976.88) * mm]});
            skFitSpline(sketch, "E228", {"points": [v(308.81, 1976.88) * mm, v(299.14, 1966.25) * mm, v(285.63, 1948.54) * mm, v(278.79, 1937.52) * mm]});
            skFitSpline(sketch, "E229", {"points": [v(278.79, 1937.52) * mm, v(271.95, 1926.5) * mm, v(259.13, 1914.74) * mm, v(250.3, 1911.39) * mm]});
            skFitSpline(sketch, "E230", {"points": [v(250.3, 1911.39) * mm, v(225.67, 1902.02) * mm, v(216.4, 1886.7) * mm, v(221.11, 1863.14) * mm]});
            skFitSpline(sketch, "E231", {"points": [v(221.11, 1863.14) * mm, v(224.08, 1848.3) * mm, v(231.61, 1839.58) * mm, v(246.23, 1834.06) * mm]});
            skFitSpline(sketch, "E232", {"points": [v(246.23, 1834.06) * mm, v(290.62, 1817.3) * mm, v(261.32, 1767.59) * mm, v(207.05, 1767.59) * mm]});
            skFitSpline(sketch, "E233", {"points": [v(207.05, 1767.59) * mm, v(163.5, 1767.59) * mm, v(153.79, 1754.07) * mm, v(177.29, 1726.14) * mm]});
            skFitSpline(sketch, "E234", {"points": [v(177.29, 1726.14) * mm, v(190, 1711.04) * mm, v(195.42, 1696.1) * mm, v(195.42, 1676.27) * mm]});
            skFitSpline(sketch, "E235", {"points": [v(195.42, 1676.27) * mm, v(195.42, 1657.05) * mm, v(200.03, 1643.78) * mm, v(209.76, 1634.97) * mm]});
            skFitSpline(sketch, "E236", {"points": [v(209.76, 1634.97) * mm, v(232.3, 1614.57) * mm, v(227.18, 1599.93) * mm, v(181.09, 1553.11) * mm]});
            skFitSpline(sketch, "E237", {"points": [v(181.09, 1553.11) * mm, v(153.02, 1524.61) * mm, v(138.07, 1503.55) * mm, v(138.07, 1492.52) * mm]});
            skFitSpline(sketch, "E238", {"points": [v(138.07, 1492.52) * mm, v(138.07, 1483.22) * mm, v(132.1, 1467.92) * mm, v(124.8, 1458.52) * mm]});
            skFitSpline(sketch, "E239", {"points": [v(124.8, 1458.52) * mm, v(117.51, 1449.12) * mm, v(112.88, 1437.57) * mm, v(114.52, 1432.86) * mm]});
            skFitSpline(sketch, "E240", {"points": [v(114.52, 1432.86) * mm, v(119.4, 1418.86) * mm, v(102.01, 1393.24) * mm, v(65.18, 1360.13) * mm]});
            skFitSpline(sketch, "E241", {"points": [v(65.18, 1360.13) * mm, v(46.13, 1343) * mm, v(30.55, 1325.83) * mm, v(30.55, 1321.98) * mm]});
            skFitSpline(sketch, "E242", {"points": [v(30.55, 1321.98) * mm, v(30.55, 1318.13) * mm, v(40.23, 1300.91) * mm, v(52.05, 1283.72) * mm]});
            skFitSpline(sketch, "E243", {"points": [v(52.05, 1283.72) * mm, v(63.88, 1266.53) * mm, v(73.56, 1249.7) * mm, v(73.56, 1246.3) * mm]});
            skFitSpline(sketch, "E244", {"points": [v(73.56, 1246.3) * mm, v(73.56, 1232.89) * mm, v(102.45, 1184.56) * mm, v(116.25, 1174.9) * mm]});
            skFitSpline(sketch, "E245", {"points": [v(116.25, 1174.9) * mm, v(124.31, 1169.25) * mm, v(130.9, 1158.55) * mm, v(130.9, 1151.12) * mm]});
            skFitSpline(sketch, "E246", {"points": [v(130.9, 1151.12) * mm, v(130.9, 1143.7) * mm, v(134.13, 1135.62) * mm, v(138.07, 1133.18) * mm]});
            skFitSpline(sketch, "E247", {"points": [v(138.07, 1133.18) * mm, v(147.42, 1127.4) * mm, v(147.3, 1098.69) * mm, v(137.9, 1089.29) * mm]});
            skFitSpline(sketch, "E248", {"points": [v(137.9, 1089.29) * mm, v(132.9, 1084.28) * mm, v(135.18, 1077.77) * mm, v(145.07, 1068.82) * mm]});
            skFitSpline(sketch, "E249", {"points": [v(145.07, 1068.82) * mm, v(153.05, 1061.6) * mm, v(159.58, 1049.14) * mm, v(159.58, 1041.14) * mm]});
            skFitSpline(sketch, "E250", {"points": [v(159.58, 1041.14) * mm, v(159.58, 1019.4) * mm, v(131.58, 993.4) * mm, v(108.15, 993.4) * mm]});
            skFitSpline(sketch, "E251", {"points": [v(108.15, 993.4) * mm, v(84.76, 993.4) * mm, v(83.19, 988.97) * mm, v(100, 970.4) * mm]});
            skFitSpline(sketch, "E252", {"points": [v(100, 970.4) * mm, v(110.25, 959.07) * mm, v(110.8, 953.45) * mm, v(103.58, 933.49) * mm]});
            skFitSpline(sketch, "E253", {"points": [v(103.58, 933.49) * mm, v(98.9, 920.54) * mm, v(95.06, 903.63) * mm, v(95.06, 895.92) * mm]});
            skFitSpline(sketch, "E254", {"points": [v(95.06, 895.92) * mm, v(95.06, 877.93) * mm, v(58, 845.3) * mm, v(30.76, 839.32) * mm]});
            skFitSpline(sketch, "E255", {"points": [v(30.76, 839.32) * mm, v(18.98, 836.73) * mm, v(7.76, 828.6) * mm, v(5.3, 820.86) * mm]});
            skFitSpline(sketch, "E256", {"points": [v(5.3, 820.86) * mm, v(2.88, 813.25) * mm, v(-1.75, 807.02) * mm, v(-5, 807.02) * mm]});
            skFitSpline(sketch, "E257", {"points": [v(-5, 807.02) * mm, v(-8.25, 807.02) * mm, v(-12.9, 799.08) * mm, v(-15.34, 789.37) * mm]});
            skFitSpline(sketch, "E258", {"points": [v(-15.34, 789.37) * mm, v(-21.39, 765.26) * mm, v(-78.44, 723.22) * mm, v(-113.05, 717.37) * mm]});
            skFitSpline(sketch, "E259", {"points": [v(-113.05, 717.37) * mm, v(-128.65, 714.74) * mm, v(-143.24, 709.64) * mm, v(-145.46, 706.04) * mm]});
            skFitSpline(sketch, "E260", {"points": [v(-145.46, 706.04) * mm, v(-147.69, 702.44) * mm, v(-163.12, 699.5) * mm, v(-179.75, 699.5) * mm]});
            skFitSpline(sketch, "E261", {"points": [v(-179.75, 699.5) * mm, v(-216.22, 699.5) * mm, v(-241.85, 683.3) * mm, v(-241.85, 660.24) * mm]});
            skFitSpline(sketch, "E262", {"points": [v(-241.85, 660.24) * mm, v(-241.85, 630.25) * mm, v(-250.47, 619.3) * mm, v(-287.74, 601.95) * mm]});
            skFitSpline(sketch, "E263", {"points": [v(-287.74, 601.95) * mm, v(-330.56, 582.02) * mm, v(-368.05, 580) * mm, v(-386.45, 596.66) * mm]});
            skFitSpline(sketch, "E264", {"points": [v(-386.45, 596.66) * mm, v(-398.22, 607.3) * mm, v(-400.84, 607.4) * mm, v(-412.1, 597.61) * mm]});
            skFitSpline(sketch, "E265", {"points": [v(-412.1, 597.61) * mm, v(-419, 591.61) * mm, v(-442.74, 584.68) * mm, v(-464.86, 582.22) * mm]});
            skFitSpline(sketch, "E266", {"points": [v(-464.86, 582.22) * mm, v(-520.75, 576) * mm, v(-554.79, 560.2) * mm, v(-568.2, 534.28) * mm]});
            skFitSpline(sketch, "E267", {"points": [v(-568.2, 534.28) * mm, v(-574.39, 522.3) * mm, v(-586.88, 509.11) * mm, v(-595.94, 504.98) * mm]});
            skFitSpline(sketch, "E268", {"points": [v(-595.94, 504.98) * mm, v(-611.44, 497.92) * mm, v(-612.02, 495.29) * mm, v(-605.66, 460.49) * mm]});
            skFitSpline(sketch, "E269", {"points": [v(-605.66, 460.49) * mm, v(-600.86, 434.17) * mm, v(-601.55, 412.47) * mm, v(-608.06, 385.24) * mm]});
            skFitSpline(sketch, "E270", {"points": [v(-608.06, 385.24) * mm, v(-616.62, 349.4) * mm, v(-616.14, 345.02) * mm, v(-600.44, 316.29) * mm]});
            skFitSpline(sketch, "E271", {"points": [v(-600.44, 316.29) * mm, v(-591.22, 299.41) * mm, v(-585.66, 280.45) * mm, v(-588.08, 274.14) * mm]});
            skFitSpline(sketch, "E272", {"points": [v(-588.08, 274.14) * mm, v(-590.5, 267.83) * mm, v(-589.4, 260.77) * mm, v(-585.63, 258.44) * mm]});
            skFitSpline(sketch, "E273", {"points": [v(-585.63, 258.44) * mm, v(-572.7, 250.44) * mm, v(-578.36, 219.93) * mm, v(-594.37, 211.36) * mm]});
            skFitSpline(sketch, "E274", {"points": [v(-591.64, 193.4) * mm, v(-558.83, 176.21) * mm, v(-559.57, 140.5) * mm, v(-593.09, 123.78) * mm]});
            skFitSpline(sketch, "E275", {"points": [v(-593.09, 123.78) * mm, v(-611.54, 114.58) * mm, v(-635.56, 71.76) * mm, v(-653.16, 16.7) * mm]});
            skFitSpline(sketch, "E276", {"points": [v(-653.16, 16.7) * mm, v(-655.37, 9.8) * mm, v(-663.46, 4.15) * mm, v(-671.14, 4.15) * mm]});
            skFitSpline(sketch, "E277", {"points": [v(-671.14, 4.15) * mm, v(-698.4, 4.15) * mm, v(-695.58, -28.52) * mm, v(-667.4, -39.23) * mm]});
            skFitSpline(sketch, "E278", {"points": [v(-667.4, -39.23) * mm, v(-657.29, -43.08) * mm, v(-650.45, -51.52) * mm, v(-650.45, -60.19) * mm]});
            skFitSpline(sketch, "E279", {"points": [v(-650.45, -60.19) * mm, v(-650.45, -75.26) * mm, v(-673.78, -103.37) * mm, v(-686.3, -103.37) * mm]});
            skFitSpline(sketch, "E280", {"points": [v(-686.3, -103.37) * mm, v(-690.24, -103.37) * mm, v(-693.47, -114.2) * mm, v(-693.47, -127.45) * mm]});
            skFitSpline(sketch, "E281", {"points": [v(-693.47, -127.45) * mm, v(-693.47, -148.68) * mm, v(-698.12, -154.62) * mm, v(-732.9, -177.7) * mm]});
            skFitSpline(sketch, "E282", {"points": [v(-732.9, -177.7) * mm, v(-766.2, -199.82) * mm, v(-772.32, -207.24) * mm, v(-772.32, -225.54) * mm]});
            skFitSpline(sketch, "E283", {"points": [v(-772.32, -225.54) * mm, v(-772.32, -238.17) * mm, v(-776.8, -248.91) * mm, v(-783.07, -251.32) * mm]});
            skFitSpline(sketch, "E284", {"points": [v(-783.07, -251.32) * mm, v(-791.26, -254.46) * mm, v(-793.82, -267.85) * mm, v(-793.82, -307.56) * mm]});
            skFitSpline(sketch, "E285", {"points": [v(-793.82, -307.56) * mm, v(-793.82, -345.15) * mm, v(-796.82, -362.17) * mm, v(-804.58, -368.6) * mm]});
            skFitSpline(sketch, "E286", {"points": [v(-804.58, -368.6) * mm, v(-810.49, -373.52) * mm, v(-815.33, -385.07) * mm, v(-815.33, -394.28) * mm]});
            skFitSpline(sketch, "E287", {"points": [v(-815.33, -394.28) * mm, v(-815.33, -413.15) * mm, v(-838.33, -436.97) * mm, v(-881.17, -462.47) * mm]});
            skFitSpline(sketch, "E288", {"points": [v(-881.17, -462.47) * mm, v(-935.18, -494.62) * mm, v(-951.11, -512.98) * mm, v(-958.33, -551.4) * mm]});
            skFitSpline(sketch, "E289", {"points": [v(-958.33, -551.4) * mm, v(-962.04, -571.12) * mm, v(-974.78, -606.1) * mm, v(-986.65, -629.15) * mm]});
            skFitSpline(sketch, "E290", {"points": [v(-986.65, -629.15) * mm, v(-1001.62, -658.2) * mm, v(-1007.03, -677.12) * mm, v(-1004.3, -690.82) * mm]});
            skFitSpline(sketch, "E291", {"points": [v(-1004.3, -690.82) * mm, v(-1000.1, -711.82) * mm, v(-1011.37, -724.16) * mm, v(-1058.35, -750) * mm]});
            skFitSpline(sketch, "E292", {"points": [v(-1058.35, -750) * mm, v(-1076.8, -760.14) * mm, v(-1080.56, -766.56) * mm, v(-1080.56, -787.98) * mm]});
            skFitSpline(sketch, "E293", {"points": [v(-1080.56, -787.98) * mm, v(-1080.56, -802.16) * mm, v(-1085.5, -823.3) * mm, v(-1091.53, -834.98) * mm]});
            skFitSpline(sketch, "E294", {"points": [v(-1091.53, -834.98) * mm, v(-1099.59, -850.56) * mm, v(-1100.54, -859.85) * mm, v(-1095.12, -870) * mm]});
            skFitSpline(sketch, "E295", {"points": [v(-1095.12, -870) * mm, v(-1091.05, -877.58) * mm, v(-1087.73, -894.87) * mm, v(-1087.73, -908.41) * mm]});
            skFitSpline(sketch, "E296", {"points": [v(-1087.73, -908.41) * mm, v(-1087.73, -948.48) * mm, v(-1108.26, -1054.24) * mm, v(-1121.37, -1081.75) * mm]});
            skFitSpline(sketch, "E297", {"points": [v(-1121.37, -1081.75) * mm, v(-1133.23, -1106.6) * mm, v(-1133.14, -1107.51) * mm, v(-1117.8, -1118.26) * mm]});
            skFitSpline(sketch, "E298", {"points": [v(-1117.8, -1118.26) * mm, v(-1100.84, -1130.13) * mm, v(-1097, -1156.37) * mm, v(-1110.27, -1169.64) * mm]});
            skFitSpline(sketch, "E299", {"points": [v(-1110.27, -1169.64) * mm, v(-1116.43, -1175.8) * mm, v(-1116.34, -1183) * mm, v(-1109.9, -1198.52) * mm]});
            skFitSpline(sketch, "E300", {"points": [v(-1109.9, -1198.52) * mm, v(-1102.71, -1215.9) * mm, v(-1103.7, -1225.49) * mm, v(-1116.12, -1258.67) * mm]});
            skFitSpline(sketch, "E301", {"points": [v(-1116.12, -1258.67) * mm, v(-1124.24, -1280.38) * mm, v(-1138.62, -1305.4) * mm, v(-1148.07, -1314.29) * mm]});
            skFitSpline(sketch, "E302", {"points": [v(-1148.07, -1314.29) * mm, v(-1161.65, -1327.04) * mm, v(-1166.4, -1341.2) * mm, v(-1170.75, -1381.77) * mm]});
            skFitSpline(sketch, "E303", {"points": [v(-1170.75, -1381.77) * mm, v(-1173.78, -1410.02) * mm, v(-1175.5, -1440.07) * mm, v(-1174.58, -1448.57) * mm]});
            skFitSpline(sketch, "E304", {"points": [v(-1174.58, -1448.57) * mm, v(-1173.66, -1457.06) * mm, v(-1176.32, -1466.12) * mm, v(-1180.5, -1468.7) * mm]});
            skFitSpline(sketch, "E305", {"points": [v(-1180.5, -1468.7) * mm, v(-1191.46, -1475.48) * mm, v(-1189.82, -1509.89) * mm, v(-1177.72, -1527.16) * mm]});
            skFitSpline(sketch, "E306", {"points": [v(-1177.72, -1527.16) * mm, v(-1171.15, -1536.55) * mm, v(-1167.6, -1558.36) * mm, v(-1168, -1586.77) * mm]});
            skFitSpline(sketch, "E307", {"points": [v(-1168, -1586.77) * mm, v(-1168.52, -1624) * mm, v(-1171.78, -1635.33) * mm, v(-1187.2, -1653.66) * mm]});
            skFitSpline(sketch, "E308", {"points": [v(-1187.2, -1653.66) * mm, v(-1207.29, -1677.53) * mm, v(-1208.52, -1701.35) * mm, v(-1191.09, -1728.57) * mm]});
            skFitSpline(sketch, "E309", {"points": [v(-1191.09, -1728.57) * mm, v(-1177.17, -1750.3) * mm, v(-1178.33, -1770.97) * mm, v(-1194.1, -1782.18) * mm]});
            skFitSpline(sketch, "E310", {"points": [v(-1194.1, -1782.18) * mm, v(-1201.35, -1787.33) * mm, v(-1209.4, -1800.14) * mm, v(-1212, -1810.65) * mm]});
            skFitSpline(sketch, "E311", {"points": [v(-1212, -1810.65) * mm, v(-1215.85, -1826.19) * mm, v(-1224.45, -1832.33) * mm, v(-1257.97, -1843.47) * mm]});
            skFitSpline(sketch, "E312", {"points": [v(-1302.78, -1904.43) * mm, v(-1305.42, -1939.16) * mm, v(-1310.92, -1957.83) * mm, v(-1323.55, -1974.9) * mm]});
            skFitSpline(sketch, "E313", {"points": [v(-1323.55, -1974.9) * mm, v(-1339.81, -1996.87) * mm, v(-1340.3, -2000.45) * mm, v(-1332.63, -2041.71) * mm]});
            skFitSpline(sketch, "E314", {"points": [v(-1332.63, -2041.71) * mm, v(-1328.17, -2065.69) * mm, v(-1317.87, -2093.4) * mm, v(-1309.75, -2103.3) * mm]});
            skFitSpline(sketch, "E315", {"points": [v(-1309.75, -2103.3) * mm, v(-1301.62, -2113.2) * mm, v(-1291.23, -2130.06) * mm, v(-1286.64, -2140.77) * mm]});
            skFitSpline(sketch, "E316", {"points": [v(-1286.64, -2140.77) * mm, v(-1280.35, -2155.48) * mm, v(-1274.65, -2159.33) * mm, v(-1263.35, -2156.5) * mm]});
            skFitSpline(sketch, "E317", {"points": [v(-1263.35, -2156.5) * mm, v(-1244.96, -2151.88) * mm, v(-1228.86, -2168.93) * mm, v(-1217.14, -2205.42) * mm]});
            skFitSpline(sketch, "E318", {"points": [v(-1217.14, -2205.42) * mm, v(-1212.42, -2220.15) * mm, v(-1205.65, -2234) * mm, v(-1202.12, -2236.18) * mm]});
            skFitSpline(sketch, "E319", {"points": [v(-1202.12, -2236.18) * mm, v(-1196.58, -2239.6) * mm, v(-685.13, -2258.98) * mm, v(-263.36, -2271.75) * mm]});
            skFitSpline(sketch, "E320", {"points": [v(-263.36, -2271.75) * mm, v(-190.42, -2273.96) * mm, v(-98.48, -2277.23) * mm, v(-59.06, -2279.02) * mm]});
            skFitSpline(sketch, "E321", {"points": [v(-59.06, -2279.02) * mm, v(-19.63, -2280.8) * mm, v(114.24, -2284.38) * mm, v(238.43, -2286.96) * mm]});
            skFitSpline(sketch, "E322", {"points": [v(238.43, -2286.96) * mm, v(362.63, -2289.54) * mm, v(465.58, -2292.84) * mm, v(467.23, -2294.29) * mm]});
            skFitSpline(sketch, "E323", {"points": [v(467.23, -2294.29) * mm, v(476.4, -2302.36) * mm, v(490.5, -2293.4) * mm, v(514.3, -2264.34) * mm]});
            skSolve(sketch);
        }
        {
            var Q0;
            Q0=makeQuery(id+"F0.imprint","IMPRINT",FACE,{"disambiguationData":[TD([[makeQuery(id+"F0.imprint","IMPRINT",EDGE,{"derivedFrom":sQuery(id+"F0.wireOp",EDGE,"E0")}),1.0]])]});
            var Q1;
            Q1=makeQuery(id+"F0.imprint","IMPRINT",FACE,{"disambiguationData":[TD([[makeQuery(id+"F0.imprint","IMPRINT",EDGE,{"derivedFrom":sQuery(id+"F0.wireOp",EDGE,"E11")}),1.0]])]});
            extrude(context, id + "F1", {"entities" : qUnion([Q0, Q1]), "depth" : 25.4 * mm, "offsetDistance" : 25.4 * mm});
        }
    });
